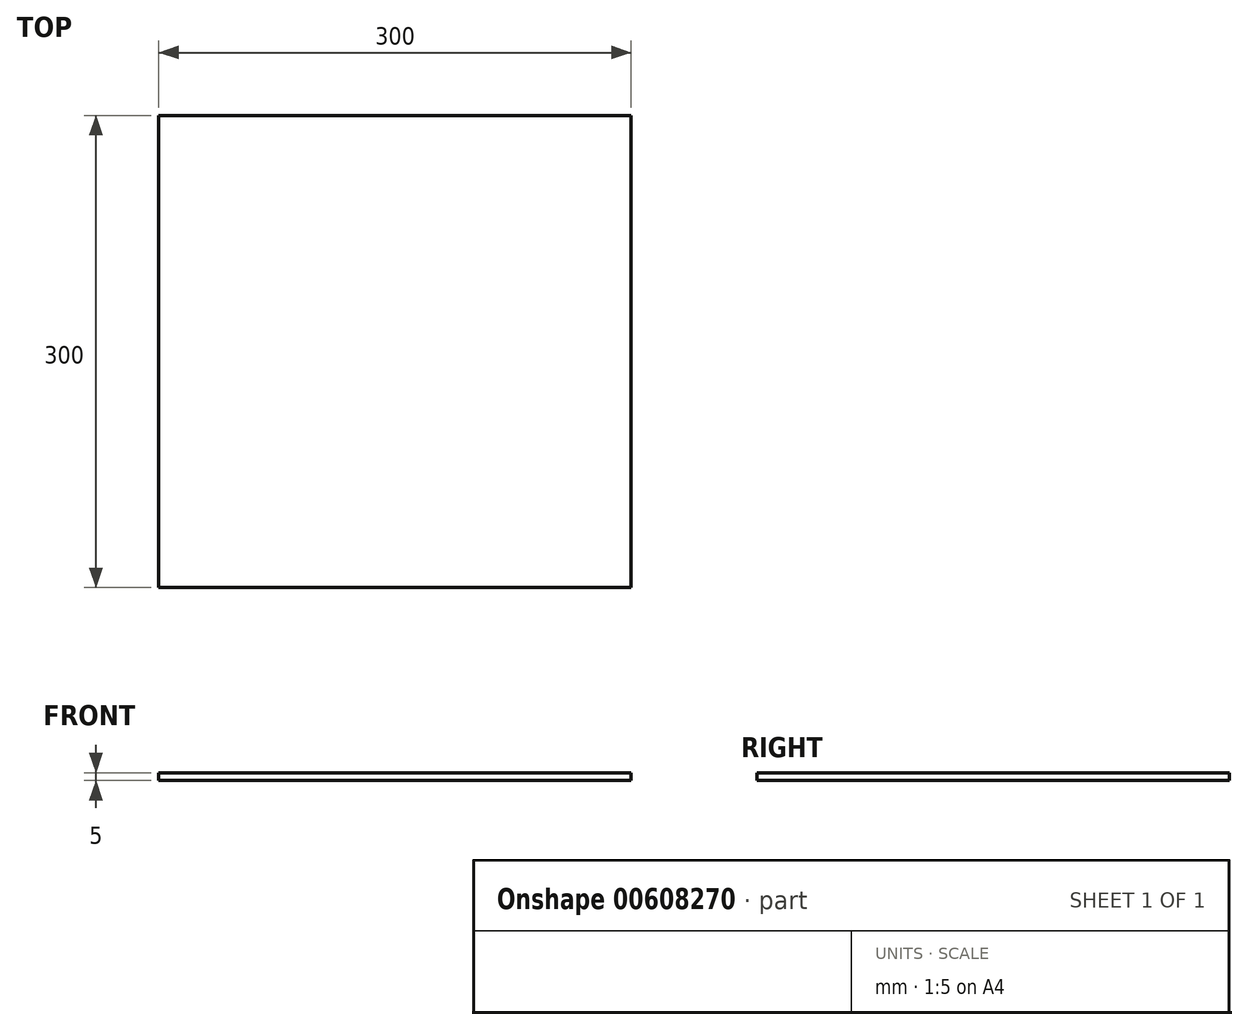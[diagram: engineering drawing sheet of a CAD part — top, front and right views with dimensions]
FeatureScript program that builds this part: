
annotation { "Feature Type Name" : "Feature", "Feature Type Description" : "" }
export const myFeature = defineFeature(function(context is Context, id is Id, definition is map)
    precondition{}
    {
        {
            var Q0;
            Q0=qCreatedBy(makeId("Top.planeOp"),FACE);
            var sketch = newSketch(context, id + "F0", { "sketchPlane" : qUnion([Q0])});
            skLineSegment(sketch, "E0.bottom", {"start": v(-150, 150) * mm, "end": v(150, 150) * mm});
            skLineSegment(sketch, "E0.top", {"start": v(-150, -150) * mm, "end": v(150, -150) * mm});
            skLineSegment(sketch, "E0.left", {"start": v(-150, 150) * mm, "end": v(-150, -150) * mm});
            skLineSegment(sketch, "E0.right", {"start": v(150, 150) * mm, "end": v(150, -150) * mm});
            skPoint(sketch, "E0.middle", {"position": v(0, 0) * mm});
            skSolve(sketch);
        }
        {
            var Q0;
            Q0 = qSketchRegion(id + "F0", true);
            extrude(context, id + "F1", {"entities" : qUnion([Q0]), "depth" : 5 * mm, "offsetDistance" : 25 * mm});
        }
    });
